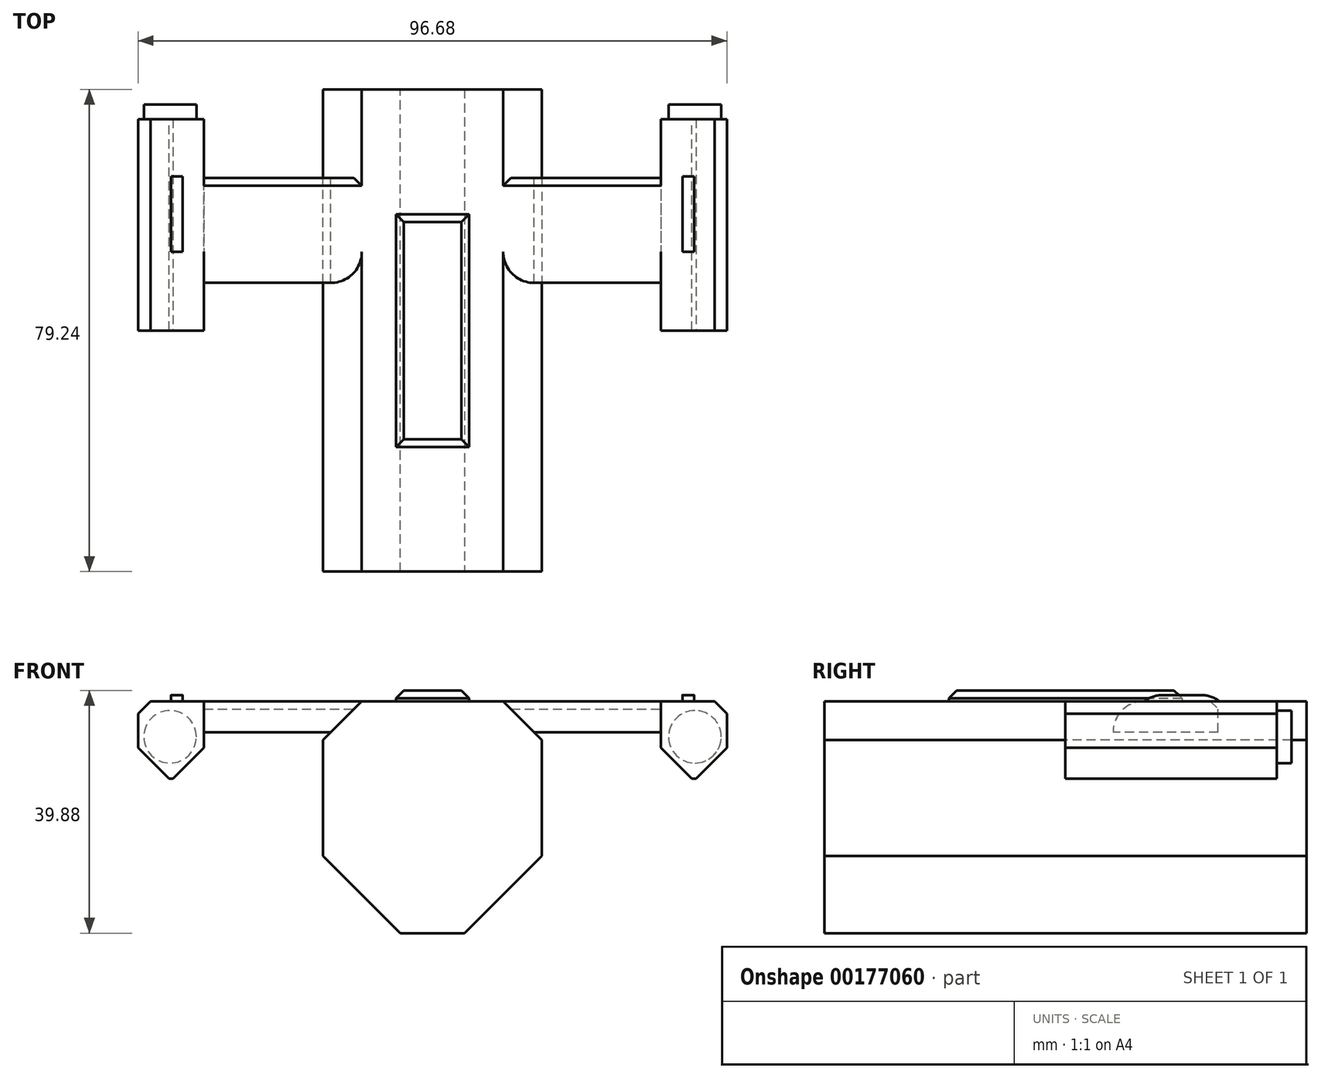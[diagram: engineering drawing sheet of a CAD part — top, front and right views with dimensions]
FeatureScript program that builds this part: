
annotation { "Feature Type Name" : "Feature", "Feature Type Description" : "" }
export const myFeature = defineFeature(function(context is Context, id is Id, definition is map)
    precondition{}
    {
        {
            var Q0;
            Q0=qCreatedBy(makeId("Top.planeOp"),FACE);
            var sketch = newSketch(context, id + "F0", { "sketchPlane" : qUnion([Q0])});
            skLineSegment(sketch, "E0.bottom", {"start": v(17.96, 39.62) * mm, "end": v(-17.96, 39.62) * mm});
            skLineSegment(sketch, "E0.top", {"start": v(17.96, -39.62) * mm, "end": v(-17.96, -39.62) * mm});
            skLineSegment(sketch, "E0.left", {"start": v(17.96, 39.62) * mm, "end": v(17.96, -39.62) * mm});
            skLineSegment(sketch, "E0.right", {"start": v(-17.96, 39.62) * mm, "end": v(-17.96, -39.62) * mm});
            skPoint(sketch, "E0.middle", {"position": v(0, 0) * mm});
            skLineSegment(sketch, "E1.bottom", {"start": v(-9.23, -39.62) * mm, "end": v(9.23, -39.62) * mm});
            skLineSegment(sketch, "E1.top", {"start": v(-9.23, -52.37) * mm, "end": v(9.23, -52.37) * mm});
            skLineSegment(sketch, "E1.left", {"start": v(-9.23, -39.62) * mm, "end": v(-9.23, -52.37) * mm});
            skLineSegment(sketch, "E1.right", {"start": v(9.23, -39.62) * mm, "end": v(9.23, -52.37) * mm});
            skPoint(sketch, "E1.middle", {"position": v(0, -46) * mm});
            skArc(sketch, "E2", {"start": v(-9.07, -52.37) * mm, "mid": v(0, -61.45) * mm, "end": v(9.07, -52.37) * mm});
            skLineSegment(sketch, "E3.bottom", {"start": v(37.54, 25.08) * mm, "end": v(17.96, 25.08) * mm});
            skLineSegment(sketch, "E3.top", {"start": v(37.54, 7.82) * mm, "end": v(17.96, 7.82) * mm});
            skLineSegment(sketch, "E3.left", {"start": v(37.54, 25.08) * mm, "end": v(37.54, 7.82) * mm});
            skLineSegment(sketch, "E3.right", {"start": v(-37.54, 25.08) * mm, "end": v(-37.54, 7.82) * mm});
            skPoint(sketch, "E3.middle", {"position": v(0, 16.45) * mm});
            skLineSegment(sketch, "E4.trimOffspring", {"start": v(-17.96, 25.08) * mm, "end": v(-37.54, 25.08) * mm});
            skLineSegment(sketch, "E5.trimOffspring", {"start": v(-17.96, 7.82) * mm, "end": v(-37.54, 7.82) * mm});
            skLineSegment(sketch, "E6.bottom", {"start": v(37.54, 0) * mm, "end": v(48.34, 0) * mm});
            skLineSegment(sketch, "E6.top", {"start": v(37.54, 34.73) * mm, "end": v(48.34, 34.73) * mm});
            skLineSegment(sketch, "E6.left", {"start": v(37.54, 0) * mm, "end": v(37.54, 34.73) * mm});
            skLineSegment(sketch, "E6.right", {"start": v(48.34, 0) * mm, "end": v(48.34, 34.73) * mm});
            skLineSegment(sketch, "E7.bottom", {"start": v(-37.54, 0) * mm, "end": v(-48.34, 0) * mm});
            skLineSegment(sketch, "E7.top", {"start": v(-37.54, 34.73) * mm, "end": v(-48.34, 34.73) * mm});
            skLineSegment(sketch, "E7.left", {"start": v(-37.54, 0) * mm, "end": v(-37.54, 34.73) * mm});
            skLineSegment(sketch, "E7.right", {"start": v(-48.34, 0) * mm, "end": v(-48.34, 34.73) * mm});
            skLineSegment(sketch, "E8.bottom", {"start": v(39.8, 34.73) * mm, "end": v(46.07, 34.73) * mm});
            skLineSegment(sketch, "E8.top", {"start": v(39.8, 38.11) * mm, "end": v(46.07, 38.11) * mm});
            skLineSegment(sketch, "E8.left", {"start": v(39.8, 34.73) * mm, "end": v(39.8, 38.11) * mm});
            skLineSegment(sketch, "E8.right", {"start": v(46.07, 34.73) * mm, "end": v(46.07, 38.11) * mm});
            skLineSegment(sketch, "E9.bottom", {"start": v(-46.33, 34.73) * mm, "end": v(-40.05, 34.73) * mm});
            skLineSegment(sketch, "E9.top", {"start": v(-46.33, 37.94) * mm, "end": v(-40.05, 37.94) * mm});
            skLineSegment(sketch, "E9.left", {"start": v(-46.33, 34.73) * mm, "end": v(-46.33, 37.94) * mm});
            skLineSegment(sketch, "E9.right", {"start": v(-40.05, 34.73) * mm, "end": v(-40.05, 37.94) * mm});
            skSolve(sketch);
        }
        {
            var Q0;
            {var subQ1=sQuery(id+"F0.wireOp",EDGE,"E0.bottom");Q0=makeQuery(id+"F0.imprint","IMPRINT",FACE,{"disambiguationData":[TD([[makeQuery(id+"F0.imprint","IMPRINT",EDGE,{"derivedFrom":subQ1}),1.0]])]});}
            extrude(context, id + "F1", {"entities" : qUnion([Q0]), "oppositeDirection" : true, "depth" : 38.1 * mm});
        }
        {
            var Q0;
            {var subQ0=sQuery(id+"F0.wireOp",EDGE,"E4.trimOffspring");Q0=makeQuery(id+"F0.imprint","IMPRINT",FACE,{"disambiguationData":[TD([[makeQuery(id+"F0.imprint","IMPRINT",EDGE,{"derivedFrom":subQ0}),1.0]])]});}
            var Q1;
            {var subQ0=sQuery(id+"F0.wireOp",EDGE,"E3.bottom");Q1=makeQuery(id+"F0.imprint","IMPRINT",FACE,{"disambiguationData":[TD([[makeQuery(id+"F0.imprint","IMPRINT",EDGE,{"derivedFrom":subQ0}),1.0]])]});}
            extrude(context, id + "F2", {"entities" : qUnion([Q0, Q1]), "operationType" : NewBodyOperationType.ADD, "oppositeDirection" : true, "depth" : 5.08 * mm});
        }
        {
            var Q0;
            {var subQ2=sQuery(id+"F0.wireOp",EDGE,"E7.bottom");Q0=makeQuery(id+"F0.imprint","IMPRINT",FACE,{"disambiguationData":[TD([[makeQuery(id+"F0.imprint","IMPRINT",EDGE,{"derivedFrom":subQ2}),-1.0]])]});}
            var Q1;
            {var subQ2=sQuery(id+"F0.wireOp",EDGE,"E6.bottom");Q1=makeQuery(id+"F0.imprint","IMPRINT",FACE,{"disambiguationData":[TD([[makeQuery(id+"F0.imprint","IMPRINT",EDGE,{"derivedFrom":subQ2}),1.0]])]});}
            extrude(context, id + "F3", {"entities" : qUnion([Q0, Q1]), "operationType" : NewBodyOperationType.ADD, "oppositeDirection" : true, "depth" : 12.7 * mm});
        }
        {
            var Q0;
            Q0=makeQuery(id+"F1.opExtrude","CAP_EDGE",EDGE,{"disambiguationData":[OSD([sQuery(id+"F0.wireOp",EDGE,"E0.right")])],"isStart":false});
            var Q1;
            Q1=makeQuery(id+"F1.opExtrude","CAP_EDGE",EDGE,{"disambiguationData":[OSD([sQuery(id+"F0.wireOp",EDGE,"E0.left")])],"isStart":false});
            chamfer(context, id + "F4", {"entities" : qUnion([Q0, Q1]), "width" : 12.7 * mm, "tangentPropagation" : true});
        }
        {
            var Q0;
            Q0=makeQuery(id+"F2.opExtrude","CAP_EDGE",EDGE,{"disambiguationData":[OSD([sQuery(id+"F0.wireOp",EDGE,"E5.trimOffspring")])],"isStart":true});
            var Q1;
            Q1=makeQuery(id+"F2.opExtrude","CAP_EDGE",EDGE,{"disambiguationData":[OSD([sQuery(id+"F0.wireOp",EDGE,"E3.top")])],"isStart":true});
            fillet(context, id + "F5", {"entities" : qUnion([Q0, Q1]), "radius" : 5.08 * mm, "tangentPropagation" : true, "allowEdgeOverflow" : false});
        }
        {
            var Q0;
            {var subQ3=sQuery(id+"F0.wireOp",EDGE,"E0.right");var subQ4=sQuery(id+"F0.wireOp",EDGE,"E5.trimOffspring");Q0=makeQuery(id+"F2.boolean.opBoolean","SPLIT",EDGE,{"disambiguationData":[TD([makeQuery(id+"F2.opExtrude","SWEPT_FACE",FACE,{"disambiguationData":[OSD([subQ4])]})])],"derivedFrom":makeQuery(id+"F1.opExtrude","CAP_EDGE",EDGE,{"disambiguationData":[OSD([subQ3])],"isStart":true})});}
            var Q1;
            {var subQ0=sQuery(id+"F0.wireOp",EDGE,"E3.top");var subQ1=sQuery(id+"F0.wireOp",EDGE,"E0.left");Q1=makeQuery(id+"F2.boolean.opBoolean","SPLIT",EDGE,{"disambiguationData":[TD([makeQuery(id+"F2.opExtrude","SWEPT_FACE",FACE,{"disambiguationData":[OSD([subQ0])]})])],"derivedFrom":makeQuery(id+"F1.opExtrude","CAP_EDGE",EDGE,{"disambiguationData":[OSD([subQ1])],"isStart":true})});}
            chamfer(context, id + "F6", {"entities" : qUnion([Q0, Q1]), "width" : 6.35 * mm, "tangentPropagation" : true});
        }
        {
            var Q0;
            Q0=makeQuery(id+"F3.opExtrude","SWEPT_FACE",FACE,{"disambiguationData":[OSD([sQuery(id+"F0.wireOp",EDGE,"E6.top"),sQuery(id+"F0.wireOp",EDGE,"E8.bottom")])]});
            var sketch = newSketch(context, id + "F7", { "sketchPlane" : qUnion([Q0])});
            skCircle(sketch, "E10", {"center": v(-43.1, -5.84) * mm, "radius": 4.32 * mm});
            skCircle(sketch, "E11", {"center": v(43.1, -5.84) * mm, "radius": 4.32 * mm});
            skSolve(sketch);
        }
        {
            var Q0;
            Q0=makeQuery(id+"F7.imprint","IMPRINT",FACE,{"disambiguationData":[TD([[makeQuery(id+"F7.imprint","IMPRINT",EDGE,{"derivedFrom":sQuery(id+"F7.wireOp",EDGE,"E10")}),1.0]])]});
            var Q1;
            Q1=makeQuery(id+"F7.imprint","IMPRINT",FACE,{"disambiguationData":[TD([[makeQuery(id+"F7.imprint","IMPRINT",EDGE,{"derivedFrom":sQuery(id+"F7.wireOp",EDGE,"E11")}),1.0]])]});
            extrude(context, id + "F8", {"entities" : qUnion([Q0, Q1]), "operationType" : NewBodyOperationType.ADD, "depth" : 2.41 * mm});
        }
        {
            var Q0;
            Q0=makeQuery(id+"F3.opExtrude","CAP_EDGE",EDGE,{"disambiguationData":[OSD([sQuery(id+"F0.wireOp",EDGE,"E7.right")])],"isStart":false});
            var Q1;
            Q1=makeQuery(id+"F3.opExtrude","CAP_EDGE",EDGE,{"disambiguationData":[OSD([sQuery(id+"F0.wireOp",EDGE,"E7.left")])],"isStart":false});
            var Q2;
            Q2=makeQuery(id+"F3.opExtrude","CAP_EDGE",EDGE,{"disambiguationData":[OSD([sQuery(id+"F0.wireOp",EDGE,"E6.right")])],"isStart":false});
            var Q3;
            Q3=makeQuery(id+"F3.opExtrude","CAP_EDGE",EDGE,{"disambiguationData":[OSD([sQuery(id+"F0.wireOp",EDGE,"E6.left")])],"isStart":false});
            chamfer(context, id + "F9", {"entities" : qUnion([Q0, Q1, Q2, Q3]), "width" : 5.08 * mm, "tangentPropagation" : true});
        }
        {
            var Q0;
            Q0=makeQuery(id+"F3.opExtrude","CAP_EDGE",EDGE,{"disambiguationData":[OSD([sQuery(id+"F0.wireOp",EDGE,"E6.right")])],"isStart":true});
            var Q1;
            Q1=makeQuery(id+"F3.opExtrude","CAP_EDGE",EDGE,{"disambiguationData":[OSD([sQuery(id+"F0.wireOp",EDGE,"E7.right")])],"isStart":true});
            chamfer(context, id + "F10", {"entities" : qUnion([Q0, Q1]), "width" : 2.03 * mm, "tangentPropagation" : true});
        }
        {
            var Q0;
            Q0=makeQuery(id+"F2.opExtrude","CAP_EDGE",EDGE,{"disambiguationData":[OSD([sQuery(id+"F0.wireOp",EDGE,"E3.bottom")])],"isStart":true});
            var Q1;
            Q1=makeQuery(id+"F2.opExtrude","CAP_EDGE",EDGE,{"disambiguationData":[OSD([sQuery(id+"F0.wireOp",EDGE,"E4.trimOffspring")])],"isStart":true});
            chamfer(context, id + "F11", {"entities" : qUnion([Q0, Q1]), "width" : 1.27 * mm, "tangentPropagation" : true});
        }
        {
            var Q0;
            {var subQ1=sQuery(id+"F0.wireOp",EDGE,"E0.bottom");Q0=makeQuery(id+"F0.imprint","IMPRINT",FACE,{"disambiguationData":[TD([[makeQuery(id+"F0.imprint","IMPRINT",EDGE,{"derivedFrom":subQ1}),1.0]])]});}
            var sketch = newSketch(context, id + "F12", { "sketchPlane" : qUnion([Q0])});
            skLineSegment(sketch, "E12.bottom", {"start": v(-6, 19.12) * mm, "end": v(6, 19.12) * mm});
            skLineSegment(sketch, "E12.top", {"start": v(-6, -19.12) * mm, "end": v(6, -19.12) * mm});
            skLineSegment(sketch, "E12.left", {"start": v(-6, 19.12) * mm, "end": v(-6, -19.12) * mm});
            skLineSegment(sketch, "E12.right", {"start": v(6, 19.12) * mm, "end": v(6, -19.12) * mm});
            skPoint(sketch, "E12.middle", {"position": v(0, 0) * mm});
            skLineSegment(sketch, "E13.bottom", {"start": v(-42.94, 25.3) * mm, "end": v(-41.04, 25.3) * mm});
            skLineSegment(sketch, "E13.top", {"start": v(-42.94, 12.93) * mm, "end": v(-41.04, 12.93) * mm});
            skLineSegment(sketch, "E13.left", {"start": v(-42.94, 25.3) * mm, "end": v(-42.94, 12.93) * mm});
            skLineSegment(sketch, "E13.right", {"start": v(-41.04, 25.3) * mm, "end": v(-41.04, 12.93) * mm});
            skPoint(sketch, "E13.middle", {"position": v(-42, 19.12) * mm});
            skLineSegment(sketch, "E14.bottom", {"start": v(41.04, 25.3) * mm, "end": v(42.94, 25.3) * mm});
            skLineSegment(sketch, "E14.top", {"start": v(41.04, 12.93) * mm, "end": v(42.94, 12.93) * mm});
            skLineSegment(sketch, "E14.left", {"start": v(41.04, 25.3) * mm, "end": v(41.04, 12.93) * mm});
            skLineSegment(sketch, "E14.right", {"start": v(42.94, 25.3) * mm, "end": v(42.94, 12.93) * mm});
            skPoint(sketch, "E14.middle", {"position": v(42, 19.12) * mm});
            skSolve(sketch);
        }
        {
            var Q0;
            Q0=makeQuery(id+"F12.imprint","IMPRINT",FACE,{"disambiguationData":[TD([[makeQuery(id+"F12.imprint","IMPRINT",EDGE,{"derivedFrom":sQuery(id+"F12.wireOp",EDGE,"E12.bottom")}),-1.0]])]});
            extrude(context, id + "F13", {"entities" : qUnion([Q0]), "operationType" : NewBodyOperationType.ADD, "depth" : 1.78 * mm});
        }
        {
            var Q0;
            Q0=makeQuery(id+"F12.imprint","IMPRINT",FACE,{"disambiguationData":[TD([[makeQuery(id+"F12.imprint","IMPRINT",EDGE,{"derivedFrom":sQuery(id+"F12.wireOp",EDGE,"E13.bottom")}),-1.0]])]});
            var Q1;
            Q1=makeQuery(id+"F12.imprint","IMPRINT",FACE,{"disambiguationData":[TD([[makeQuery(id+"F12.imprint","IMPRINT",EDGE,{"derivedFrom":sQuery(id+"F12.wireOp",EDGE,"E14.bottom")}),-1.0]])]});
            extrude(context, id + "F14", {"entities" : qUnion([Q0, Q1]), "operationType" : NewBodyOperationType.ADD, "depth" : 1.02 * mm});
        }
        {
            var Q0;
            Q0=makeQuery(id+"F13.opExtrude","CAP_EDGE",EDGE,{"disambiguationData":[OSD([sQuery(id+"F12.wireOp",EDGE,"E12.right")])],"isStart":false});
            var Q1;
            Q1=makeQuery(id+"F13.opExtrude","CAP_EDGE",EDGE,{"disambiguationData":[OSD([sQuery(id+"F12.wireOp",EDGE,"E12.top")])],"isStart":false});
            var Q2;
            Q2=makeQuery(id+"F13.opExtrude","CAP_EDGE",EDGE,{"disambiguationData":[OSD([sQuery(id+"F12.wireOp",EDGE,"E12.left")])],"isStart":false});
            var Q3;
            Q3=makeQuery(id+"F13.opExtrude","CAP_EDGE",EDGE,{"disambiguationData":[OSD([sQuery(id+"F12.wireOp",EDGE,"E12.bottom")])],"isStart":false});
            chamfer(context, id + "F15", {"entities" : qUnion([Q0, Q1, Q2, Q3]), "width" : 1.27 * mm, "tangentPropagation" : true});
        }
        {
            var Q0;
            Q0=makeQuery(id+"F14.opExtrude","CAP_EDGE",EDGE,{"disambiguationData":[OSD([sQuery(id+"F12.wireOp",EDGE,"E14.top")])],"isStart":false});
            var Q1;
            Q1=makeQuery(id+"F14.opExtrude","CAP_EDGE",EDGE,{"disambiguationData":[OSD([sQuery(id+"F12.wireOp",EDGE,"E14.bottom")])],"isStart":false});
            var Q2;
            Q2=makeQuery(id+"F14.opExtrude","CAP_EDGE",EDGE,{"disambiguationData":[OSD([sQuery(id+"F12.wireOp",EDGE,"E13.top")])],"isStart":false});
            var Q3;
            Q3=makeQuery(id+"F14.opExtrude","CAP_EDGE",EDGE,{"disambiguationData":[OSD([sQuery(id+"F12.wireOp",EDGE,"E13.bottom")])],"isStart":false});
            fillet(context, id + "F16", {"entities" : qUnion([Q0, Q1, Q2, Q3]), "radius" : 5.08 * mm, "tangentPropagation" : true, "allowEdgeOverflow" : false});
        }
    });
